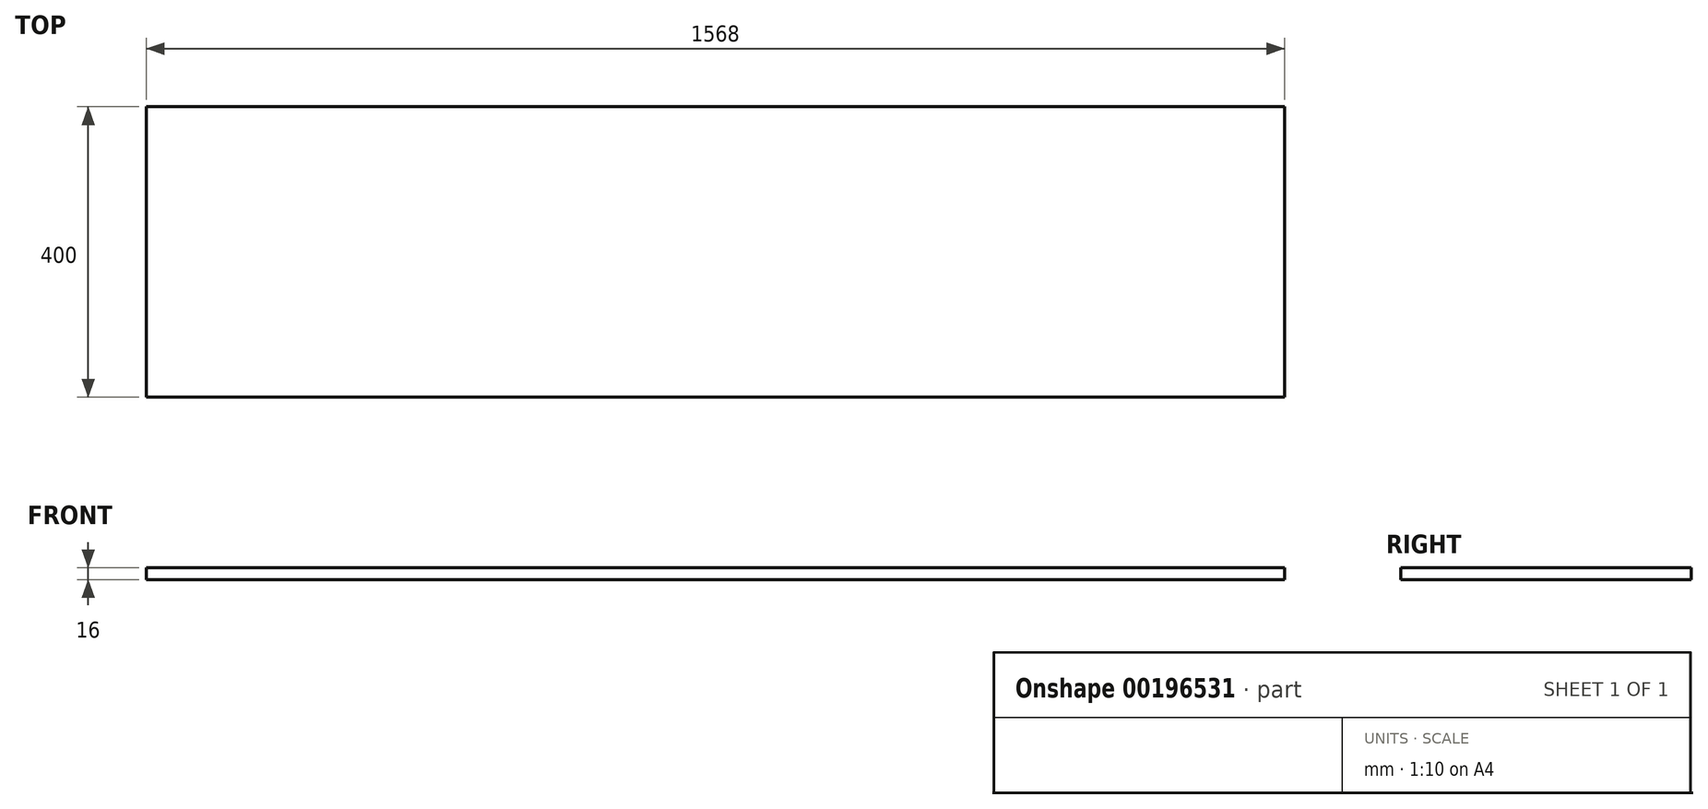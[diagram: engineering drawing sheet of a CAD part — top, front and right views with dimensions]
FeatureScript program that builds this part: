
annotation { "Feature Type Name" : "Feature", "Feature Type Description" : "" }
export const myFeature = defineFeature(function(context is Context, id is Id, definition is map)
    precondition{}
    {
        {
            var Q0;
            Q0=qCreatedBy(makeId("Top.planeOp"),FACE);
            var sketch = newSketch(context, id + "F0", { "sketchPlane" : qUnion([Q0])});
            skLineSegment(sketch, "E0.bottom", {"start": v(-864.34, -235.28) * mm, "end": v(703.66, -235.28) * mm});
            skLineSegment(sketch, "E0.top", {"start": v(-864.34, 164.72) * mm, "end": v(703.66, 164.72) * mm});
            skLineSegment(sketch, "E0.left", {"start": v(-864.34, -235.28) * mm, "end": v(-864.34, 164.72) * mm});
            skLineSegment(sketch, "E0.right", {"start": v(703.66, -235.28) * mm, "end": v(703.66, 164.72) * mm});
            skSolve(sketch);
        }
        {
            var Q0;
            Q0=makeQuery(id+"F0.imprint","IMPRINT",FACE,{"disambiguationData":[TD([[makeQuery(id+"F0.imprint","IMPRINT",EDGE,{"derivedFrom":sQuery(id+"F0.wireOp",EDGE,"E0.bottom")}),1.0]])]});
            extrude(context, id + "F1", {"entities" : qUnion([Q0]), "depth" : 16 * mm});
        }
    });
